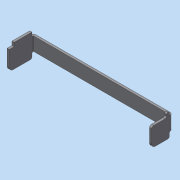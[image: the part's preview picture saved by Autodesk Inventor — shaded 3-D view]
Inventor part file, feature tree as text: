
AUTODESK INVENTOR PART (.ipt)
format: ipt  version: 2020 (Build 240168000, 168)  size: 209,920 bytes
history: native  units: mm
features: other x3, extrude x1
ambient origin geometry x8: Origin, YZ Plane, XZ Plane, XY Plane, X Axis, Y Axis, Z Axis, Center Point
bodies: Body1 (feature_tree)
feature tree (4):
  other  "實體1"
  extrude  "擠出1"  Depth=125.0mm
  other  "折彎零件1"
  other  "折彎零件2"
